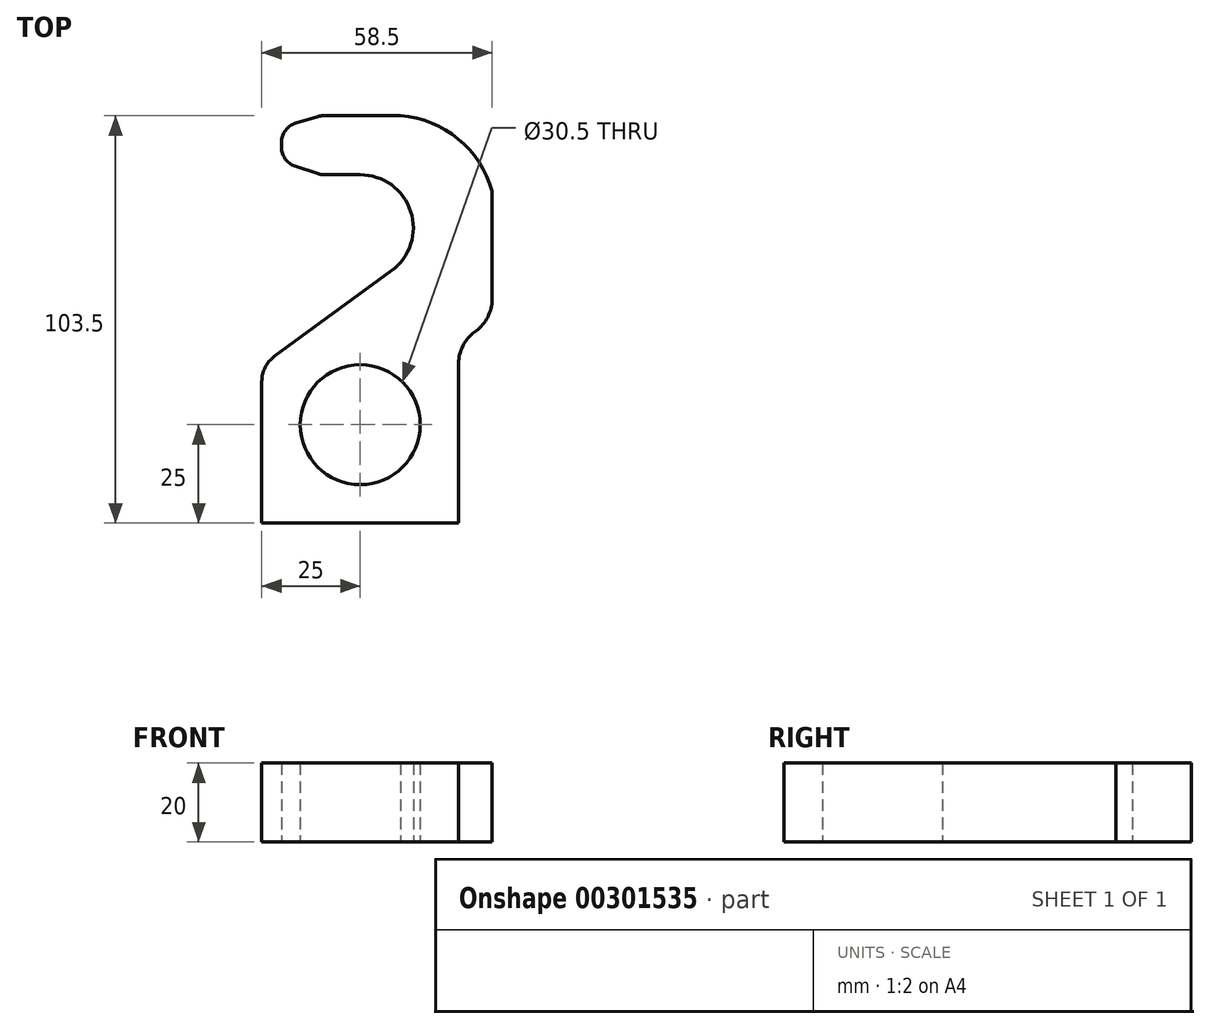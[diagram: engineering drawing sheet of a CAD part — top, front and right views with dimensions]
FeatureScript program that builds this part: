
annotation { "Feature Type Name" : "Feature", "Feature Type Description" : "" }
export const myFeature = defineFeature(function(context is Context, id is Id, definition is map)
    precondition{}
    {
        {
            var Q0;
            Q0=qCreatedBy(makeId("Top.planeOp"),FACE);
            var sketch = newSketch(context, id + "F0", { "sketchPlane" : qUnion([Q0])});
            skArc(sketch, "E0", {"start": v(7.97, -10.9) * mm, "mid": v(12.83, 4.2) * mm, "end": v(0, 13.5) * mm});
            skLineSegment(sketch, "E1", {"start": v(0, 13.5) * mm, "end": v(-9.19, 13.5) * mm});
            skLineSegment(sketch, "E2", {"start": v(-20, 20.44) * mm, "end": v(-20, 21.78) * mm});
            skLineSegment(sketch, "E3", {"start": v(-9.27, 28.5) * mm, "end": v(9.46, 28.5) * mm});
            skLineSegment(sketch, "E4", {"start": v(33.5, 5.6) * mm, "end": v(33.5, -18.12) * mm});
            skLineSegment(sketch, "E5", {"start": v(25, -75) * mm, "end": v(-25, -75) * mm});
            skLineSegment(sketch, "E6", {"start": v(-25, -75) * mm, "end": v(-25, -39.06) * mm});
            skLineSegment(sketch, "E7", {"start": v(-21.72, -32.6) * mm, "end": v(10.24, -9.24) * mm});
            skPoint(sketch, "E8.visualSharp", {"position": v(-20, 13.5) * mm});
            skPoint(sketch, "E9.visualSharp", {"position": v(-20, 28.5) * mm});
            skPoint(sketch, "E10.visualSharp", {"position": v(10.24, 28.5) * mm});
            skPoint(sketch, "E11.visualSharp", {"position": v(33.5, 9.33) * mm});
            skPoint(sketch, "E12.visualSharp", {"position": v(-25, -35) * mm});
            skArc(sketch, "E12.filletArc", {"start": v(-21.72, -32.6) * mm, "mid": v(-24.13, -35.44) * mm, "end": v(-25, -39.06) * mm});
            skLineSegment(sketch, "E13", {"start": v(25, -75) * mm, "end": v(25, -34.5) * mm});
            skLineSegment(sketch, "E14", {"start": v(29.1, -26.42) * mm, "end": v(29.4, -26.2) * mm});
            skCircle(sketch, "E15.0.5.0", {"center": v(0, -50) * mm, "radius": 15.25 * mm});
            skLineSegment(sketch, "E16", {"start": v(-10.77, 13.76) * mm, "end": v(-16.58, 15.7) * mm});
            skPoint(sketch, "E8.filletArc.end.orphan", {"position": v(-20, 13.5) * mm});
            skPoint(sketch, "E17.visualSharp", {"position": v(-20, 16.83) * mm});
            skArc(sketch, "E17.filletArc", {"start": v(-20, 20.44) * mm, "mid": v(-19.06, 17.51) * mm, "end": v(-16.58, 15.7) * mm});
            skPoint(sketch, "E18.visualSharp", {"position": v(-10, 13.5) * mm});
            skArc(sketch, "E18.filletArc", {"start": v(-10.77, 13.76) * mm, "mid": v(-9.99, 13.56) * mm, "end": v(-9.19, 13.5) * mm});
            skArc(sketch, "E19", {"start": v(33.5, 9.33) * mm, "mid": v(24.9, 22.6) * mm, "end": v(10.24, 28.5) * mm});
            skLineSegment(sketch, "E20", {"start": v(10.24, 28.5) * mm, "end": v(9.46, 28.5) * mm});
            skLineSegment(sketch, "E21", {"start": v(33.5, 5.6) * mm, "end": v(33.5, 9.33) * mm});
            skLineSegment(sketch, "E22", {"start": v(-10.7, 28.29) * mm, "end": v(-16.44, 26.57) * mm});
            skPoint(sketch, "E23.visualSharp", {"position": v(-10, 28.5) * mm});
            skArc(sketch, "E23.filletArc", {"start": v(-9.27, 28.5) * mm, "mid": v(-10, 28.45) * mm, "end": v(-10.7, 28.29) * mm});
            skPoint(sketch, "E24.visualSharp", {"position": v(-20, 25.5) * mm});
            skArc(sketch, "E24.filletArc", {"start": v(-16.44, 26.57) * mm, "mid": v(-19.01, 24.76) * mm, "end": v(-20, 21.78) * mm});
            skPoint(sketch, "E25.visualSharp", {"position": v(33.5, -23.2) * mm});
            skArc(sketch, "E25.filletArc", {"start": v(29.4, -26.2) * mm, "mid": v(32.42, -22.65) * mm, "end": v(33.5, -18.12) * mm});
            skPoint(sketch, "E26.visualSharp", {"position": v(25, -29.41) * mm});
            skArc(sketch, "E26.filletArc", {"start": v(29.1, -26.42) * mm, "mid": v(26.08, -29.96) * mm, "end": v(25, -34.5) * mm});
            skSolve(sketch);
        }
        {
            var Q0;
            Q0 = qSketchRegion(id + "F0", true);
            extrude(context, id + "F1", {"entities" : qUnion([Q0]), "depth" : 20 * mm});
        }
    });
